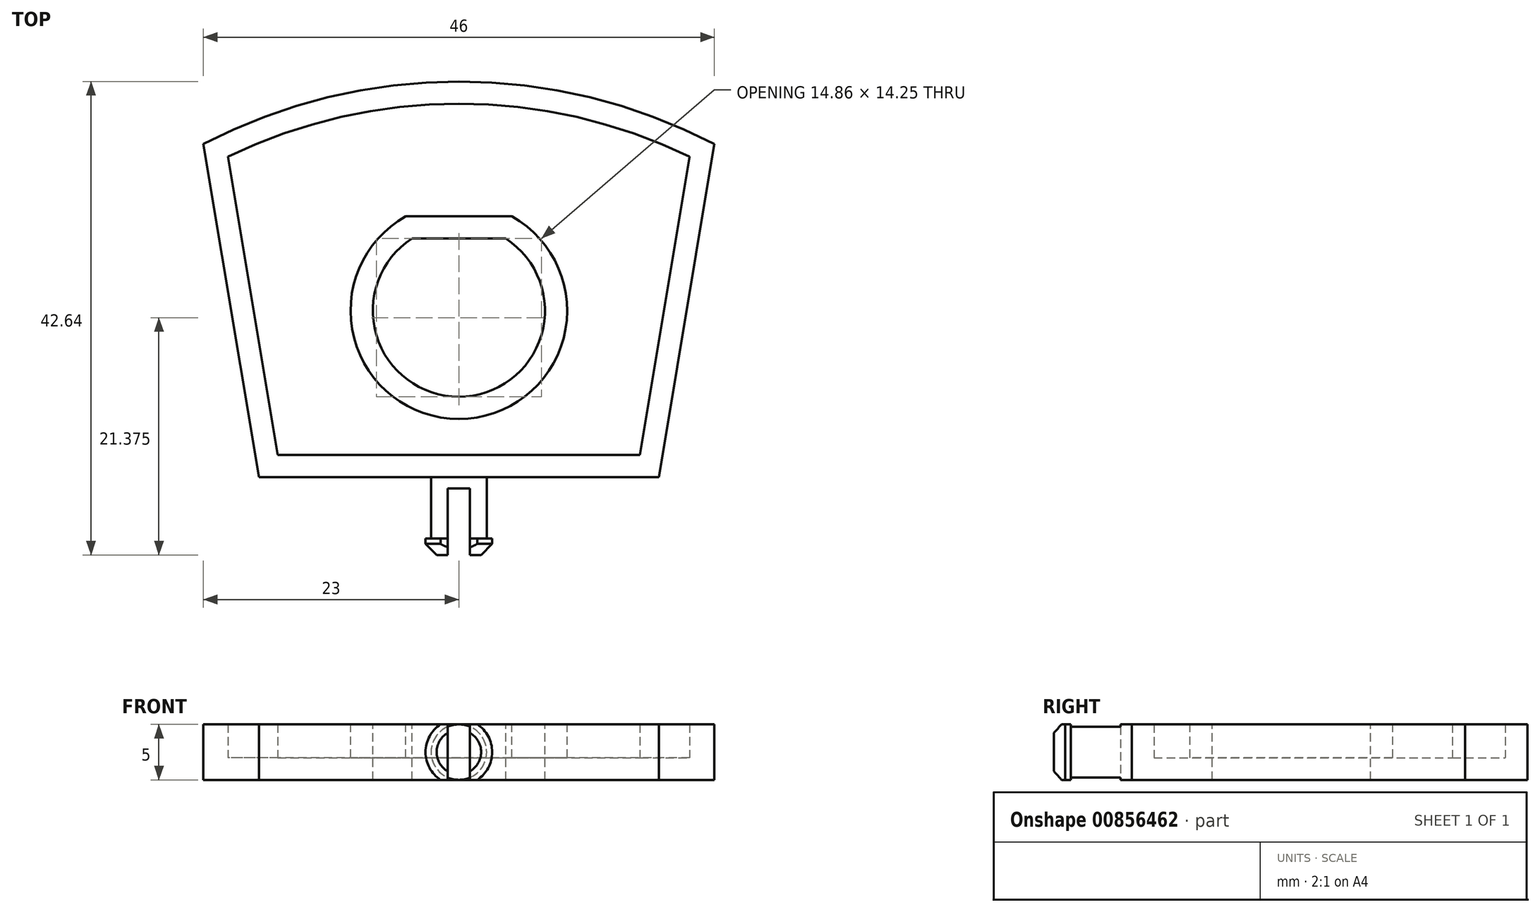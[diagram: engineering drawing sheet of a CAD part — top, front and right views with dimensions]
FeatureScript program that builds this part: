
annotation { "Feature Type Name" : "Feature", "Feature Type Description" : "" }
export const myFeature = defineFeature(function(context is Context, id is Id, definition is map)
    precondition{}
    {
        {
            var Q0;
            Q0=qCreatedBy(makeId("Top.planeOp"),FACE);
            var sketch = newSketch(context, id + "F0", { "sketchPlane" : qUnion([Q0])});
            skLineSegment(sketch, "E0", {"start": v(-18, 0) * mm, "end": v(18, 0) * mm});
            skLineSegment(sketch, "E1", {"start": v(18, 0) * mm, "end": v(23, 30) * mm});
            skLineSegment(sketch, "E2", {"start": v(-18, 0) * mm, "end": v(-23, 30) * mm});
            skArc(sketch, "E3", {"start": v(23, 30) * mm, "mid": v(0, 35.64) * mm, "end": v(-23, 30) * mm});
            skSolve(sketch);
        }
        {
            var Q0;
            Q0 = qSketchRegion(id + "F0", true);
            extrude(context, id + "F1", {"entities" : qUnion([Q0]), "endBound" : BoundingType.SYMMETRIC, "depth" : 5 * mm, "offsetDistance" : 25 * mm});
        }
        {
            var Q0;
            Q0=makeQuery(id+"F1.opExtrude","CAP_FACE",FACE,{"disambiguationData":[OSD([sQuery(id+"F0.wireOp",EDGE,"E0"),sQuery(id+"F0.wireOp",EDGE,"E1"),sQuery(id+"F0.wireOp",EDGE,"E2"),sQuery(id+"F0.wireOp",EDGE,"E3")])],"isStart":false});
            var sketch = newSketch(context, id + "F2", { "sketchPlane" : qUnion([Q0])});
            skLineSegment(sketch, "E4", {"start": v(-4.22, 21.5) * mm, "end": v(4.22, 21.5) * mm});
            skArc(sketch, "E5", {"start": v(-4.22, 21.5) * mm, "mid": v(0, 7.25) * mm, "end": v(4.22, 21.5) * mm});
            skSolve(sketch);
        }
        {
            var Q0;
            Q0 = qSketchRegion(id + "F2", true);
            extrude(context, id + "F3", {"entities" : qUnion([Q0]), "operationType" : NewBodyOperationType.REMOVE, "endBound" : BoundingType.UP_TO_NEXT, "oppositeDirection" : true, "depth" : 25 * mm, "offsetDistance" : 25 * mm});
        }
        {
            var Q0;
            Q0=makeQuery(id+"F1.opExtrude","CAP_FACE",FACE,{"disambiguationData":[OSD([sQuery(id+"F0.wireOp",EDGE,"E0"),sQuery(id+"F0.wireOp",EDGE,"E1"),sQuery(id+"F0.wireOp",EDGE,"E2"),sQuery(id+"F0.wireOp",EDGE,"E3")])],"isStart":false});
            shell(context, id + "F4", {"entities" : qUnion([Q0]), "thickness" : 2 * mm});
        }
        {
            var Q0;
            Q0=qCreatedBy(makeId("Right.planeOp"),FACE);
            var sketch = newSketch(context, id + "F5", { "sketchPlane" : qUnion([Q0])});
            skLineSegment(sketch, "E6", {"start": v(0, 0) * mm, "end": v(-7, 0) * mm});
            skLineSegment(sketch, "E7", {"start": v(-7, 0) * mm, "end": v(-7, 3) * mm});
            skLineSegment(sketch, "E8", {"start": v(-7, 3) * mm, "end": v(-5.5, 3) * mm});
            skLineSegment(sketch, "E9", {"start": v(-5.5, 3) * mm, "end": v(-5.5, 2.5) * mm});
            skLineSegment(sketch, "E10", {"start": v(-5.5, 2.5) * mm, "end": v(0, 2.5) * mm});
            skLineSegment(sketch, "E11", {"start": v(0, 2.5) * mm, "end": v(0, 0) * mm});
            skSolve(sketch);
        }
        {
            var Q0;
            Q0 = qSketchRegion(id + "F5", true);
            var Q1;
            Q1=sQuery(id+"F5.wireOp",EDGE,"E6");
            revolve(context, id + "F6", {"operationType" : NewBodyOperationType.ADD, "surfaceOperationType" : NewSurfaceOperationType.NEW, "entities" : qUnion([Q0]), "axis" : qUnion([Q1]), "revolveType" : RevolveType.FULL});
        }
        {
            var Q0;
            Q0=makeQuery(id+"F6.opRevolve","SWEPT_EDGE",EDGE,{"disambiguationData":[OSD([sQuery(id+"F5.wireOp",EDGE,"E7"),sQuery(id+"F5.wireOp",EDGE,"E8")])]});
            chamfer(context, id + "F7", {"entities" : qUnion([Q0]), "width" : 1 * mm, "tangentPropagation" : true});
        }
        {
            var Q0;
            Q0=makeQuery(id+"F6.opRevolve","SWEPT_FACE",FACE,{"disambiguationData":[OSD([sQuery(id+"F5.wireOp",EDGE,"E7")])]});
            var sketch = newSketch(context, id + "F8", { "sketchPlane" : qUnion([Q0])});
            skLineSegment(sketch, "E12.bottom", {"start": v(-25.02, 2.5) * mm, "end": v(25.22, 2.5) * mm});
            skLineSegment(sketch, "E12.top", {"start": v(-25.02, -2.5) * mm, "end": v(25.22, -2.5) * mm});
            skLineSegment(sketch, "E12.left", {"start": v(-25.02, 2.5) * mm, "end": v(-25.02, -2.5) * mm});
            skLineSegment(sketch, "E12.right", {"start": v(25.22, 2.5) * mm, "end": v(25.22, -2.5) * mm});
            skSolve(sketch);
        }
        {
            var Q0;
            Q0 = qSketchRegion(id + "F8", true);
            extrude(context, id + "F9", {"entities" : qUnion([Q0]), "operationType" : NewBodyOperationType.INTERSECT, "endBound" : BoundingType.THROUGH_ALL, "oppositeDirection" : true, "depth" : 25 * mm, "offsetDistance" : 25 * mm});
        }
        {
            var Q0;
            Q0=makeQuery(id+"F6.opRevolve","SWEPT_FACE",FACE,{"disambiguationData":[OSD([sQuery(id+"F5.wireOp",EDGE,"E7")])]});
            var sketch = newSketch(context, id + "F10", { "sketchPlane" : qUnion([Q0])});
            skLineSegment(sketch, "E13.bottom", {"start": v(-1, 3.7) * mm, "end": v(1, 3.7) * mm});
            skLineSegment(sketch, "E13.top", {"start": v(-1, -3.23) * mm, "end": v(1, -3.23) * mm});
            skLineSegment(sketch, "E13.left", {"start": v(-1, 3.7) * mm, "end": v(-1, -3.23) * mm});
            skLineSegment(sketch, "E13.right", {"start": v(1, 3.7) * mm, "end": v(1, -3.23) * mm});
            skSolve(sketch);
        }
        {
            var Q0;
            Q0 = qSketchRegion(id + "F10", true);
            extrude(context, id + "F11", {"entities" : qUnion([Q0]), "operationType" : NewBodyOperationType.REMOVE, "oppositeDirection" : true, "depth" : 6 * mm, "offsetDistance" : 25 * mm});
        }
    });
